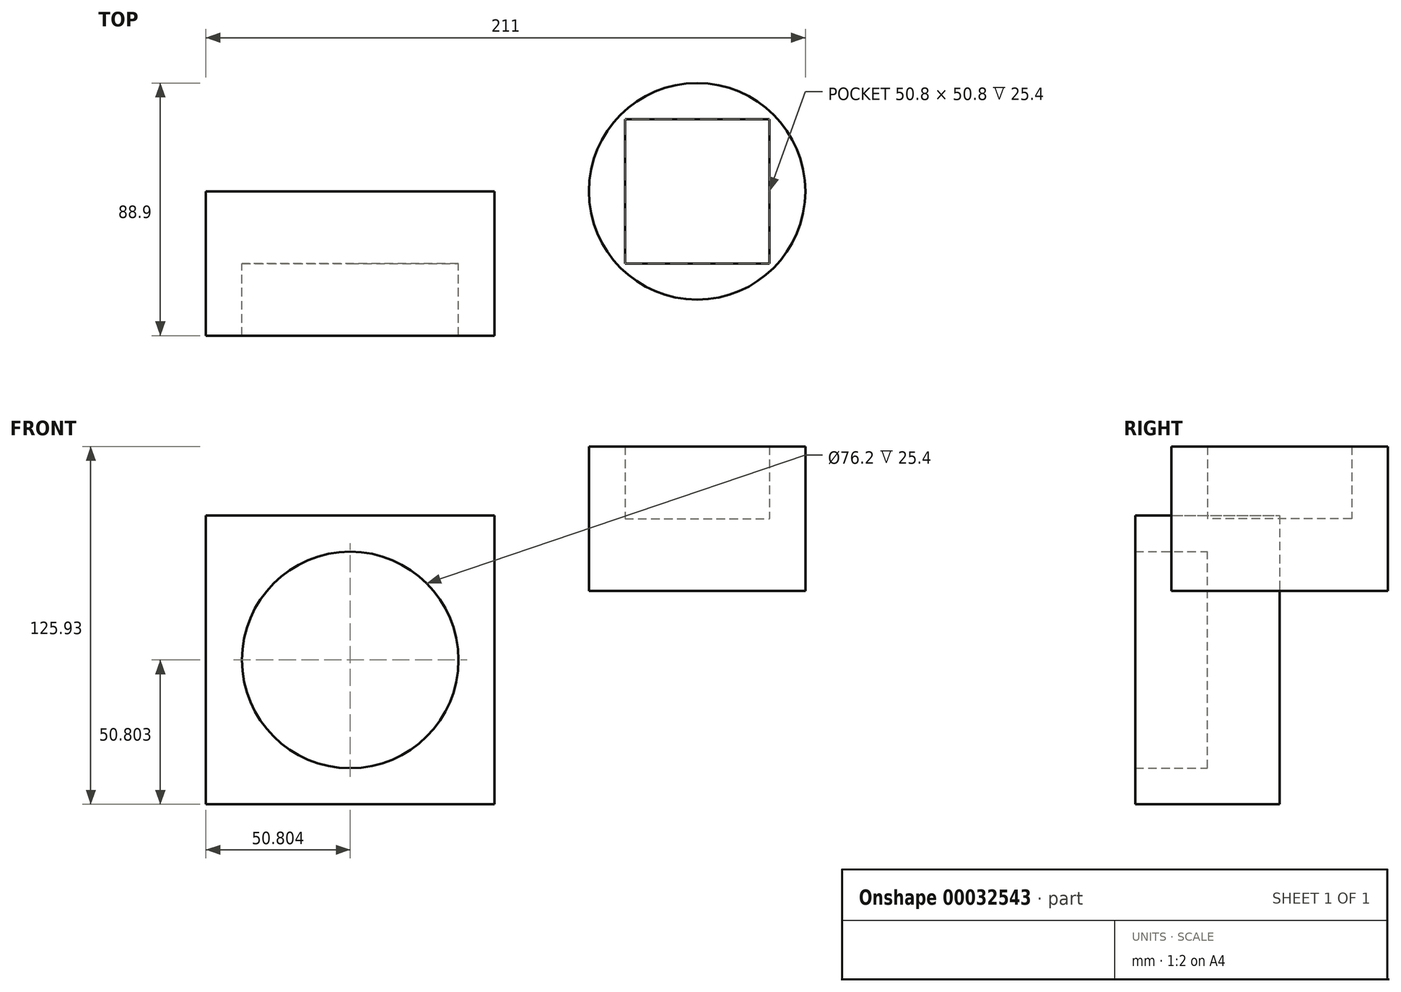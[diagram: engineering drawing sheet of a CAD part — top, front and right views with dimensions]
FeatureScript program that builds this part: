
annotation { "Feature Type Name" : "Feature", "Feature Type Description" : "" }
export const myFeature = defineFeature(function(context is Context, id is Id, definition is map)
    precondition{}
    {
        {
            var Q0;
            Q0=qCreatedBy(makeId("Top.planeOp"),FACE);
            var sketch = newSketch(context, id + "F0", { "sketchPlane" : qUnion([Q0])});
            skCircle(sketch, "E0", {"center": v(0, 0) * mm, "radius": 38.1 * mm});
            skLineSegment(sketch, "E1.rect.bottom", {"start": v(-25.4, 25.4) * mm, "end": v(25.4, 25.4) * mm});
            skLineSegment(sketch, "E1.rect.top", {"start": v(-25.4, -25.4) * mm, "end": v(25.4, -25.4) * mm});
            skLineSegment(sketch, "E1.rect.left", {"start": v(-25.4, 25.4) * mm, "end": v(-25.4, -25.4) * mm});
            skLineSegment(sketch, "E1.rect.right", {"start": v(25.4, 25.4) * mm, "end": v(25.4, -25.4) * mm});
            skSolve(sketch);
        }
        {
            var Q0;
            Q0 = qSketchRegion(id + "F0", true);
            extrude(context, id + "F1", {"entities" : qUnion([Q0]), "depth" : 50.8 * mm});
        }
        {
            var Q0;
            Q0=makeQuery(id+"F0.imprint","IMPRINT",FACE,{"disambiguationData":[TD([[makeQuery(id+"F0.imprint","IMPRINT",EDGE,{"derivedFrom":sQuery(id+"F0.wireOp",EDGE,"E1.rect.bottom")}),-1.0]])]});
            extrude(context, id + "F2", {"entities" : qUnion([Q0]), "operationType" : NewBodyOperationType.ADD, "depth" : 25.4 * mm});
        }
        {
            var Q0;
            Q0=qCreatedBy(makeId("Front.planeOp"),FACE);
            var sketch = newSketch(context, id + "F3", { "sketchPlane" : qUnion([Q0])});
            skLineSegment(sketch, "E2.rect.bottom", {"start": v(-172.9, 26.47) * mm, "end": v(-71.3, 26.47) * mm});
            skLineSegment(sketch, "E2.rect.top", {"start": v(-172.9, -75.13) * mm, "end": v(-71.3, -75.13) * mm});
            skLineSegment(sketch, "E2.rect.left", {"start": v(-172.9, 26.47) * mm, "end": v(-172.9, -75.13) * mm});
            skLineSegment(sketch, "E2.rect.right", {"start": v(-71.3, 26.47) * mm, "end": v(-71.3, -75.13) * mm});
            skPoint(sketch, "E2.rect.middle", {"position": v(-122.1, -24.33) * mm});
            skCircle(sketch, "E3", {"center": v(-122.1, -24.33) * mm, "radius": 38.1 * mm});
            skSolve(sketch);
        }
        {
            var Q0;
            Q0 = qSketchRegion(id + "F3", true);
            extrude(context, id + "F4", {"entities" : qUnion([Q0]), "depth" : 50.8 * mm});
        }
        {
            var Q0;
            Q0=makeQuery(id+"F3.imprint","IMPRINT",FACE,{"disambiguationData":[TD([[makeQuery(id+"F3.imprint","IMPRINT",EDGE,{"derivedFrom":sQuery(id+"F3.wireOp",EDGE,"E3")}),1.0]])]});
            extrude(context, id + "F5", {"entities" : qUnion([Q0]), "operationType" : NewBodyOperationType.ADD, "depth" : 25.4 * mm});
        }
    });
